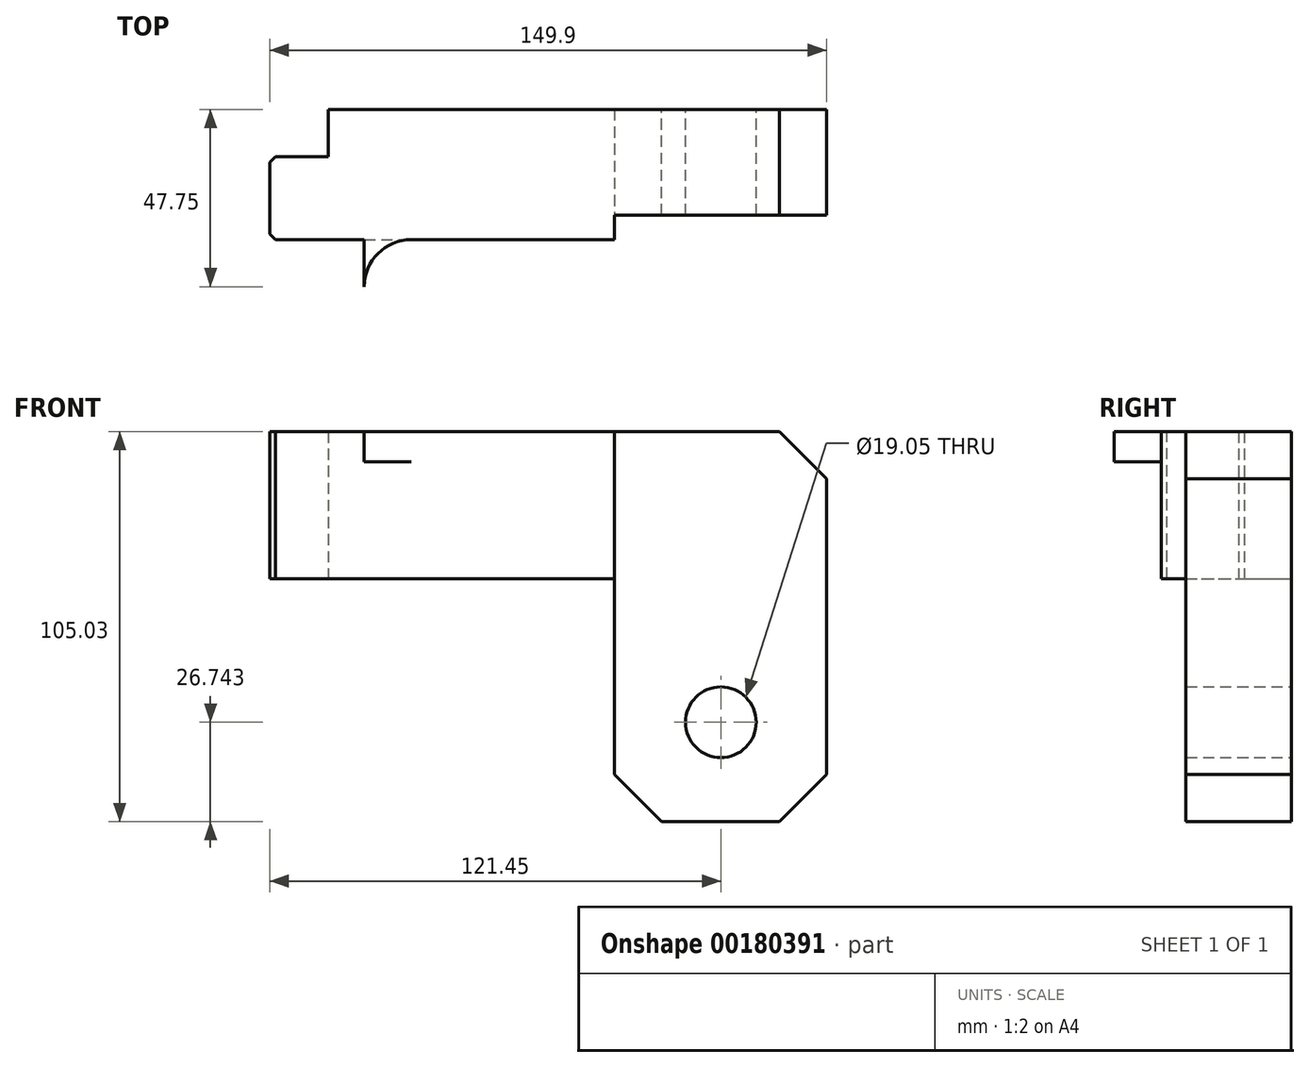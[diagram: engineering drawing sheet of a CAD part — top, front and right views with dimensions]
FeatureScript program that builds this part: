
annotation { "Feature Type Name" : "Feature", "Feature Type Description" : "" }
export const myFeature = defineFeature(function(context is Context, id is Id, definition is map)
    precondition{}
    {
        {
            var Q0;
            Q0=qCreatedBy(makeId("Front.planeOp"),FACE);
            var sketch = newSketch(context, id + "F0", { "sketchPlane" : qUnion([Q0])});
            skCircle(sketch, "E0", {"center": v(0, 0) * mm, "radius": 9.53 * mm});
            skLineSegment(sketch, "E1.bottom", {"start": v(28.45, -43.05) * mm, "end": v(-28.7, -43.05) * mm});
            skLineSegment(sketch, "E1.top", {"start": v(28.45, 53.85) * mm, "end": v(-28.7, 53.85) * mm});
            skLineSegment(sketch, "E1.left", {"start": v(28.45, -43.05) * mm, "end": v(28.45, 53.85) * mm});
            skLineSegment(sketch, "E1.right", {"start": v(-28.7, -43.05) * mm, "end": v(-28.7, 53.85) * mm});
            skLineSegment(sketch, "E2.bottom", {"start": v(-28.7, 53.85) * mm, "end": v(-98.55, 53.85) * mm});
            skLineSegment(sketch, "E2.top", {"start": v(-28.7, 15.75) * mm, "end": v(-98.55, 15.75) * mm});
            skLineSegment(sketch, "E2.left", {"start": v(-28.7, 53.85) * mm, "end": v(-28.7, 15.75) * mm});
            skLineSegment(sketch, "E2.right", {"start": v(-98.55, 53.85) * mm, "end": v(-98.55, 15.75) * mm});
            skLineSegment(sketch, "E3", {"start": v(-82.8, 15.75) * mm, "end": v(-82.8, 53.85) * mm});
            skLineSegment(sketch, "E4", {"start": v(-49.56, 15.75) * mm, "end": v(-49.56, 53.85) * mm});
            skCircle(sketch, "E5", {"center": v(0, -16.3) * mm, "radius": 9.53 * mm});
            skSolve(sketch);
        }
        {
            var Q0;
            Q0=qCreatedBy(makeId("Top.planeOp"),FACE);
            var sketch = newSketch(context, id + "F1", { "sketchPlane" : qUnion([Q0])});
            skLineSegment(sketch, "E6.bottom", {"start": v(28.45, -14.22) * mm, "end": v(-105.7, -14.22) * mm});
            skLineSegment(sketch, "E6.top", {"start": v(28.45, 14.22) * mm, "end": v(-105.7, 14.22) * mm});
            skLineSegment(sketch, "E6.left", {"start": v(28.45, -14.22) * mm, "end": v(28.45, 14.22) * mm});
            skLineSegment(sketch, "E6.right", {"start": v(-105.7, -14.22) * mm, "end": v(-105.7, 14.22) * mm});
            skLineSegment(sketch, "E7.bottom", {"start": v(-28.7, -20.83) * mm, "end": v(-121.45, -20.83) * mm});
            skLineSegment(sketch, "E7.top", {"start": v(-28.7, 1.52) * mm, "end": v(-121.45, 1.52) * mm});
            skLineSegment(sketch, "E7.left", {"start": v(-28.7, -20.83) * mm, "end": v(-28.7, 1.52) * mm});
            skLineSegment(sketch, "E7.right", {"start": v(-121.45, -20.83) * mm, "end": v(-121.45, 1.52) * mm});
            skLineSegment(sketch, "E8.bottom", {"start": v(-121.45, -20.83) * mm, "end": v(-96.05, -20.83) * mm});
            skLineSegment(sketch, "E8.top", {"start": v(-121.45, -176.28) * mm, "end": v(-96.05, -176.28) * mm});
            skLineSegment(sketch, "E8.left", {"start": v(-121.45, -20.83) * mm, "end": v(-121.45, -176.28) * mm});
            skLineSegment(sketch, "E8.right", {"start": v(-96.05, -20.83) * mm, "end": v(-96.05, -176.28) * mm});
            skArc(sketch, "E9", {"start": v(-83.35, -20.83) * mm, "mid": v(-92.33, -24.55) * mm, "end": v(-96.05, -33.53) * mm});
            skSolve(sketch);
        }
        {
            var Q0;
            Q0=qCreatedBy(makeId("Right.planeOp"),FACE);
            var sketch = newSketch(context, id + "F2", { "sketchPlane" : qUnion([Q0])});
            skLineSegment(sketch, "E10.bottom", {"start": v(-14.22, -43.05) * mm, "end": v(14.22, -43.05) * mm});
            skLineSegment(sketch, "E10.top", {"start": v(-14.22, 53.85) * mm, "end": v(14.22, 53.85) * mm});
            skLineSegment(sketch, "E10.left", {"start": v(-14.22, -43.05) * mm, "end": v(-14.22, 53.85) * mm});
            skLineSegment(sketch, "E10.right", {"start": v(14.22, -43.05) * mm, "end": v(14.22, 53.85) * mm});
            skLineSegment(sketch, "E11.bottom", {"start": v(-14.22, 53.85) * mm, "end": v(-176.28, 53.85) * mm});
            skLineSegment(sketch, "E11.top", {"start": v(-14.22, 15.75) * mm, "end": v(-176.28, 15.75) * mm});
            skLineSegment(sketch, "E11.left", {"start": v(-14.22, 53.85) * mm, "end": v(-14.22, 15.75) * mm});
            skLineSegment(sketch, "E11.right", {"start": v(-176.28, 53.85) * mm, "end": v(-176.28, 15.75) * mm});
            skLineSegment(sketch, "E12", {"start": v(-20.83, 15.75) * mm, "end": v(-20.83, 53.85) * mm});
            skLineSegment(sketch, "E13", {"start": v(-176.28, 47.04) * mm, "end": v(-20.83, 47.04) * mm});
            skCircle(sketch, "E14", {"center": v(-100.08, 47.04) * mm, "radius": 5.2 * mm});
            skCircle(sketch, "E15", {"center": v(-68.33, 47.04) * mm, "radius": 3.94 * mm});
            skCircle(sketch, "E16", {"center": v(-42.93, 47.04) * mm, "radius": 5.2 * mm});
            skCircle(sketch, "E17", {"center": v(-131.83, 47.04) * mm, "radius": 3.94 * mm});
            skCircle(sketch, "E18", {"center": v(-157.23, 47.04) * mm, "radius": 5.2 * mm});
            skPoint(sketch, "E19", {"position": v(1.52, 53.85) * mm});
            skSolve(sketch);
        }
        {
            var Q0;
            {var subQ0=sQuery(id+"F0.wireOp",EDGE,"E5");var subQ1=sQuery(id+"F0.wireOp",EDGE,"E0");var subQ2=makeQuery(id+"F0.imprint","INTERSECT",VERTEX,{"disambiguationData":[OD(0.0)],"derivedFrom":[subQ1,subQ0]});Q0=makeQuery(id+"F0.imprint","IMPRINT",FACE,{"disambiguationData":[TD([[makeQuery(id+"F0.imprint","IMPRINT",EDGE,{"disambiguationData":[TD([[subQ2,1.0]])],"derivedFrom":subQ1}),1.0]])]});}
            var Q1;
            Q1=makeQuery(id+"F0.imprint","IMPRINT",FACE,{"disambiguationData":[TD([[makeQuery(id+"F0.imprint","IMPRINT",EDGE,{"derivedFrom":sQuery(id+"F0.wireOp",EDGE,"E1.bottom")}),-1.0]])]});
            extrude(context, id + "F3", {"entities" : qUnion([Q0, Q1]), "endBound" : BoundingType.SYMMETRIC, "depth" : 28.45 * mm});
        }
        {
            var Q0;
            {var subQ2=sQuery(id+"F1.wireOp",EDGE,"E6.top");Q0=makeQuery(id+"F1.imprint","IMPRINT",FACE,{"disambiguationData":[TD([[makeQuery(id+"F1.imprint","IMPRINT",EDGE,{"derivedFrom":subQ2}),1.0]])]});}
            var Q1;
            {var subQ0=sQuery(id+"F1.wireOp",EDGE,"E6.right");var subQ1=sQuery(id+"F1.wireOp",EDGE,"E6.bottom");var subQ2=makeQuery(id+"F1.imprint","INTERSECT",VERTEX,{"derivedFrom":[subQ1,subQ0]});Q1=makeQuery(id+"F1.imprint","IMPRINT",FACE,{"disambiguationData":[TD([[makeQuery(id+"F1.imprint","IMPRINT",EDGE,{"disambiguationData":[TD([[subQ2,1.0]])],"derivedFrom":subQ1}),-1.0]])]});}
            var Q2;
            {var subQ5=sQuery(id+"F1.wireOp",EDGE,"E7.right");Q2=makeQuery(id+"F1.imprint","IMPRINT",FACE,{"disambiguationData":[TD([[makeQuery(id+"F1.imprint","IMPRINT",EDGE,{"derivedFrom":subQ5}),-1.0]])]});}
            var Q3;
            {var subQ1=sQuery(id+"F1.wireOp",EDGE,"E8.bottom");Q3=makeQuery(id+"F1.imprint","IMPRINT",FACE,{"disambiguationData":[TD([[makeQuery(id+"F1.imprint","IMPRINT",EDGE,{"derivedFrom":subQ1}),-1.0]])]});}
            var Q4;
            {var subQ3=sQuery(id+"F1.wireOp",EDGE,"E9");Q4=makeQuery(id+"F1.imprint","IMPRINT",FACE,{"disambiguationData":[TD([[makeQuery(id+"F1.imprint","IMPRINT",EDGE,{"derivedFrom":subQ3}),-1.0]])]});}
            extrude(context, id + "F4", {"entities" : qUnion([Q0, Q1, Q2, Q3, Q4]), "operationType" : NewBodyOperationType.ADD, "depth" : 61.98 * mm, "hasSecondDirection" : true, "secondDirectionOppositeDirection" : false, "secondDirectionDepth" : 22.35 * mm});
        }
        {
            var Q0;
            {var subQ0=sQuery(id+"F2.wireOp",EDGE,"E16");var subQ1=sQuery(id+"F2.wireOp",EDGE,"E13");var subQ2=makeQuery(id+"F2.imprint","INTERSECT",VERTEX,{"disambiguationData":[OD(0.0)],"derivedFrom":[subQ1,subQ0]});Q0=makeQuery(id+"F2.imprint","IMPRINT",FACE,{"disambiguationData":[TD([[makeQuery(id+"F2.imprint","IMPRINT",EDGE,{"disambiguationData":[TD([[subQ2,-1.0]])],"derivedFrom":subQ1}),-1.0]])]});}
            var Q1;
            {var subQ0=sQuery(id+"F2.wireOp",EDGE,"E16");var subQ1=sQuery(id+"F2.wireOp",EDGE,"E13");var subQ2=makeQuery(id+"F2.imprint","INTERSECT",VERTEX,{"disambiguationData":[OD(0.0)],"derivedFrom":[subQ1,subQ0]});Q1=makeQuery(id+"F2.imprint","IMPRINT",FACE,{"disambiguationData":[TD([[makeQuery(id+"F2.imprint","IMPRINT",EDGE,{"disambiguationData":[TD([[subQ2,-1.0]])],"derivedFrom":subQ1}),1.0]])]});}
            var Q2;
            {var subQ0=sQuery(id+"F2.wireOp",EDGE,"E15");var subQ1=sQuery(id+"F2.wireOp",EDGE,"E13");var subQ2=makeQuery(id+"F2.imprint","INTERSECT",VERTEX,{"disambiguationData":[OD(0.0)],"derivedFrom":[subQ1,subQ0]});Q2=makeQuery(id+"F2.imprint","IMPRINT",FACE,{"disambiguationData":[TD([[makeQuery(id+"F2.imprint","IMPRINT",EDGE,{"disambiguationData":[TD([[subQ2,-1.0]])],"derivedFrom":subQ1}),-1.0]])]});}
            var Q3;
            {var subQ0=sQuery(id+"F2.wireOp",EDGE,"E15");var subQ1=sQuery(id+"F2.wireOp",EDGE,"E13");var subQ2=makeQuery(id+"F2.imprint","INTERSECT",VERTEX,{"disambiguationData":[OD(0.0)],"derivedFrom":[subQ1,subQ0]});Q3=makeQuery(id+"F2.imprint","IMPRINT",FACE,{"disambiguationData":[TD([[makeQuery(id+"F2.imprint","IMPRINT",EDGE,{"disambiguationData":[TD([[subQ2,-1.0]])],"derivedFrom":subQ1}),1.0]])]});}
            var Q4;
            {var subQ0=sQuery(id+"F2.wireOp",EDGE,"E14");var subQ1=sQuery(id+"F2.wireOp",EDGE,"E13");var subQ2=makeQuery(id+"F2.imprint","INTERSECT",VERTEX,{"disambiguationData":[OD(0.0)],"derivedFrom":[subQ1,subQ0]});Q4=makeQuery(id+"F2.imprint","IMPRINT",FACE,{"disambiguationData":[TD([[makeQuery(id+"F2.imprint","IMPRINT",EDGE,{"disambiguationData":[TD([[subQ2,-1.0]])],"derivedFrom":subQ1}),-1.0]])]});}
            var Q5;
            {var subQ0=sQuery(id+"F2.wireOp",EDGE,"E14");var subQ1=sQuery(id+"F2.wireOp",EDGE,"E13");var subQ2=makeQuery(id+"F2.imprint","INTERSECT",VERTEX,{"disambiguationData":[OD(0.0)],"derivedFrom":[subQ1,subQ0]});Q5=makeQuery(id+"F2.imprint","IMPRINT",FACE,{"disambiguationData":[TD([[makeQuery(id+"F2.imprint","IMPRINT",EDGE,{"disambiguationData":[TD([[subQ2,-1.0]])],"derivedFrom":subQ1}),1.0]])]});}
            var Q6;
            {var subQ0=sQuery(id+"F2.wireOp",EDGE,"E17");var subQ1=sQuery(id+"F2.wireOp",EDGE,"E13");var subQ2=makeQuery(id+"F2.imprint","INTERSECT",VERTEX,{"disambiguationData":[OD(0.0)],"derivedFrom":[subQ1,subQ0]});Q6=makeQuery(id+"F2.imprint","IMPRINT",FACE,{"disambiguationData":[TD([[makeQuery(id+"F2.imprint","IMPRINT",EDGE,{"disambiguationData":[TD([[subQ2,-1.0]])],"derivedFrom":subQ1}),-1.0]])]});}
            var Q7;
            {var subQ0=sQuery(id+"F2.wireOp",EDGE,"E17");var subQ1=sQuery(id+"F2.wireOp",EDGE,"E13");var subQ2=makeQuery(id+"F2.imprint","INTERSECT",VERTEX,{"disambiguationData":[OD(0.0)],"derivedFrom":[subQ1,subQ0]});Q7=makeQuery(id+"F2.imprint","IMPRINT",FACE,{"disambiguationData":[TD([[makeQuery(id+"F2.imprint","IMPRINT",EDGE,{"disambiguationData":[TD([[subQ2,-1.0]])],"derivedFrom":subQ1}),1.0]])]});}
            var Q8;
            {var subQ0=sQuery(id+"F2.wireOp",EDGE,"E18");var subQ1=sQuery(id+"F2.wireOp",EDGE,"E13");var subQ2=makeQuery(id+"F2.imprint","INTERSECT",VERTEX,{"disambiguationData":[OD(0.0)],"derivedFrom":[subQ1,subQ0]});Q8=makeQuery(id+"F2.imprint","IMPRINT",FACE,{"disambiguationData":[TD([[makeQuery(id+"F2.imprint","IMPRINT",EDGE,{"disambiguationData":[TD([[subQ2,-1.0]])],"derivedFrom":subQ1}),-1.0]])]});}
            var Q9;
            {var subQ0=sQuery(id+"F2.wireOp",EDGE,"E18");var subQ1=sQuery(id+"F2.wireOp",EDGE,"E13");var subQ2=makeQuery(id+"F2.imprint","INTERSECT",VERTEX,{"disambiguationData":[OD(0.0)],"derivedFrom":[subQ1,subQ0]});Q9=makeQuery(id+"F2.imprint","IMPRINT",FACE,{"disambiguationData":[TD([[makeQuery(id+"F2.imprint","IMPRINT",EDGE,{"disambiguationData":[TD([[subQ2,-1.0]])],"derivedFrom":subQ1}),1.0]])]});}
            extrude(context, id + "F5", {"entities" : qUnion([Q0, Q1, Q2, Q3, Q4, Q5, Q6, Q7, Q8, Q9]), "operationType" : NewBodyOperationType.REMOVE, "endBound" : BoundingType.THROUGH_ALL, "oppositeDirection" : true, "depth" : 25.4 * mm});
        }
        {
            var Q0;
            Q0=makeQuery(id+"F3.opExtrude","SWEPT_EDGE",EDGE,{"disambiguationData":[OSD([sQuery(id+"F0.wireOp",EDGE,"E1.bottom"),sQuery(id+"F0.wireOp",EDGE,"E1.left")])]});
            var Q1;
            Q1=makeQuery(id+"F3.opExtrude","SWEPT_EDGE",EDGE,{"disambiguationData":[OSD([sQuery(id+"F0.wireOp",EDGE,"E1.bottom"),sQuery(id+"F0.wireOp",EDGE,"E1.right")])]});
            var Q2;
            Q2=makeQuery(id+"F4.opExtrude","CAP_EDGE",EDGE,{"disambiguationData":[OSD([sQuery(id+"F1.wireOp",EDGE,"E6.left")])],"isStart":false});
            chamfer(context, id + "F6", {"entities" : qUnion([Q0, Q1, Q2]), "chamferType" : ChamferType.OFFSET_ANGLE, "width" : 12.7 * mm, "oppositeDirection" : false, "angle" : 45 * degree, "tangentPropagation" : true});
        }
        {
            var Q0;
            Q0=makeQuery(id+"F4.opExtrude","SWEPT_EDGE",EDGE,{"disambiguationData":[OSD([sQuery(id+"F1.wireOp",EDGE,"E8.top"),sQuery(id+"F1.wireOp",EDGE,"E8.left")])]});
            var Q1;
            Q1=makeQuery(id+"F4.opExtrude","SWEPT_EDGE",EDGE,{"disambiguationData":[OSD([sQuery(id+"F1.wireOp",EDGE,"E7.top"),sQuery(id+"F1.wireOp",EDGE,"E7.right")])]});
            chamfer(context, id + "F7", {"entities" : qUnion([Q0, Q1]), "width" : 1.52 * mm, "tangentPropagation" : true});
        }
    });
